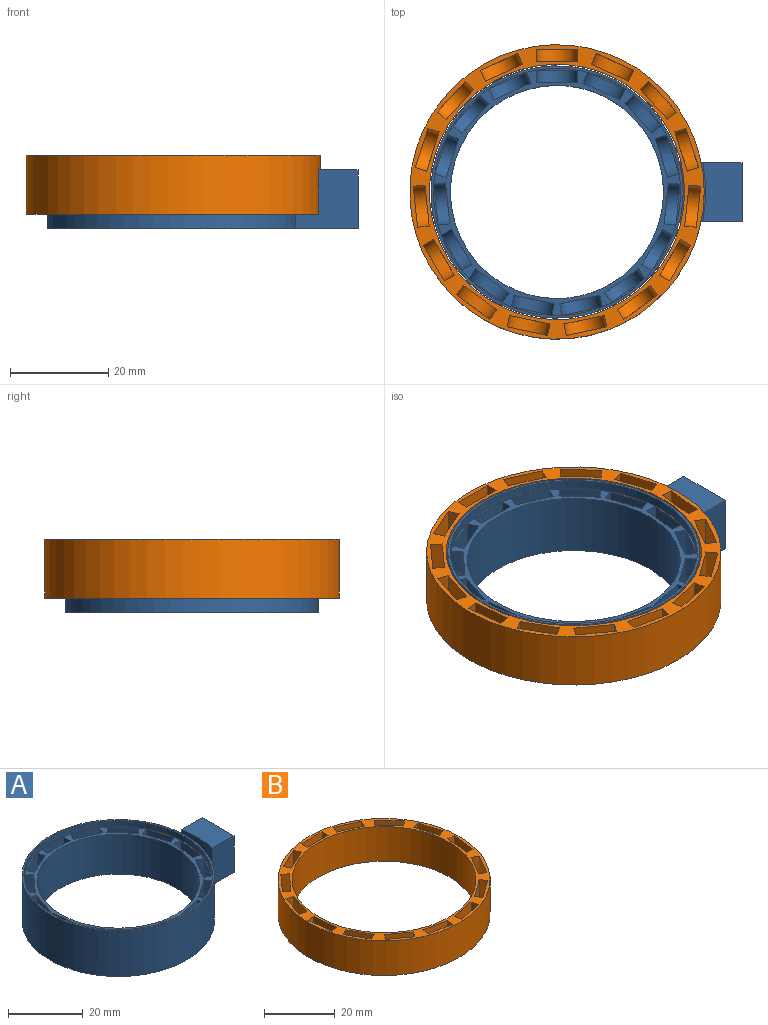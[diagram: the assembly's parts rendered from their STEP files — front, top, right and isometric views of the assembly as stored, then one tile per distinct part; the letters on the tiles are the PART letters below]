
ASSEMBLY  parts=2 mates=1
PART A: 87 faces, bbox 63.4x51.4x15 mm
  f0: cylinder r=21.7mm len=43.4mm, axis (0,0,1), area 1772.5mm2, adj f7,f10
  f1: plane 12x5.31mm, normal (0,0,1), area 55.6mm2, adj f2,f4,f6,f8
  f2: cylinder r=25.7mm len=51.4mm, axis (0,0,-1), area 2385.8mm2, adj f1,f3,f4,f6,f7
  f3: plane 51.4x51.4mm, normal (0,0,1), area 80mm2, adj f2,f11
  f4: plane 12.71x12mm, normal (0,1,0), area 110.1mm2, adj f1,f2,f5,f7,f8,f9
  f5: plane 12x12mm, normal (1,0,0), area 144mm2, adj f4,f6,f7,f9
  f6: plane 12.71x12mm, normal (0,-1,0), area 110.1mm2, adj f1,f2,f5,f7,f8,f9
  f7: plane 63.4x51.4mm, normal (0,0,-1), area 742.5mm2, adj f0,f2,f4,f5,f6
  f8: cylinder r=30.3mm len=12mm, axis (0,0,-1), area 108.7mm2, adj f1,f4,f6,f9
  f9: plane 12x8mm, normal (0,0,1), area 91.2mm2, adj f4,f5,f6,f8
  f10: plane 50.4x50.4mm, normal (0,0,1), area 213.3mm2, adj f0,f11,f13,f14,f15,f16,f18,f19
  f11: cylinder r=25.2mm len=50.4mm, axis (0,0,1), area 316.7mm2, adj f3,f10
  f12: cylinder r=4.2mm len=7.85mm, axis (0.74,0.67,0), area 31.7mm2, adj f13,f14,f15,f16
  f13: plane 9x6.24mm, normal (0.74,0.67,0), area 68mm2, adj f10,f12,f14,f16
  f14: plane 4.8x1.78mm, normal (0.67,-0.74,0), area 11.5mm2, adj f10,f12,f13,f15
  f15: plane 9x6.24mm, normal (-0.74,-0.67,0), area 68mm2, adj f10,f12,f14,f16
  f16: plane 4.8x1.78mm, normal (-0.67,0.74,0), area 11.5mm2, adj f10,f12,f13,f15
  f17: cylinder r=4.2mm len=8.73mm, axis (0.95,0.31,0), area 31.7mm2, adj f18,f19,f20,f21
  f18: plane 9x7.99mm, normal (0.95,0.31,0), area 68mm2, adj f10,f17,f19,f21
  f19: plane 4.8x2.28mm, normal (0.31,-0.95,0), area 11.5mm2, adj f10,f17,f18,f20
  f20: plane 9x7.99mm, normal (-0.95,-0.31,0), area 68mm2, adj f10,f17,f19,f21
  f21: plane 4.8x2.28mm, normal (-0.31,0.95,0), area 11.5mm2, adj f10,f17,f18,f20
  f22: cylinder r=4.2mm len=8.61mm, axis (0.99,-0.1,0), area 31.7mm2, adj f23,f24,f25,f26
  f23: plane 9x8.35mm, normal (0.99,-0.1,0), area 68mm2, adj f10,f22,f24,f26
  f24: plane 4.8x2.39mm, normal (-0.1,-0.99,0), area 11.5mm2, adj f10,f22,f23,f25
  f25: plane 9x8.35mm, normal (-0.99,0.1,0), area 68mm2, adj f10,f22,f24,f26
  f26: plane 4.8x2.39mm, normal (0.1,0.99,0), area 11.5mm2, adj f10,f22,f23,f25
  f27: cylinder r=4.2mm len=8.47mm, axis (0.87,-0.5,0), area 31.7mm2, adj f28,f29,f30,f31
  f28: plane 9x7.27mm, normal (0.87,-0.5,0), area 68mm2, adj f10,f27,f29,f31
  f29: plane 4.8x2.08mm, normal (-0.5,-0.87,0), area 11.5mm2, adj f10,f27,f28,f30
  f30: plane 9x7.27mm, normal (-0.87,0.5,0), area 68mm2, adj f10,f27,f29,f31
  f31: plane 4.8x2.08mm, normal (0.5,0.87,0), area 11.5mm2, adj f10,f27,f28,f30
  f32: cylinder r=4.2mm len=8.21mm, axis (0.59,-0.81,0), area 31.7mm2, adj f33,f34,f35,f36
  f33: plane 9x6.8mm, normal (0.59,-0.81,0), area 68mm2, adj f10,f32,f34,f36
  f34: plane 4.8x1.94mm, normal (-0.81,-0.59,0), area 11.5mm2, adj f10,f32,f33,f35
  f35: plane 9x6.8mm, normal (-0.59,0.81,0), area 68mm2, adj f10,f32,f34,f36
  f36: plane 4.8x1.94mm, normal (0.81,0.59,0), area 11.5mm2, adj f10,f32,f33,f35
  f37: cylinder r=4.2mm len=8.72mm, axis (0.21,-0.98,0), area 31.7mm2, adj f38,f39,f40,f41
  f38: plane 9x8.22mm, normal (0.21,-0.98,0), area 68mm2, adj f10,f37,f39,f41
  f39: plane 4.8x2.35mm, normal (-0.98,-0.21,0), area 11.5mm2, adj f10,f37,f38,f40
  f40: plane 9x8.22mm, normal (-0.21,0.98,0), area 68mm2, adj f10,f37,f39,f41
  f41: plane 4.8x2.35mm, normal (0.98,0.21,0), area 11.5mm2, adj f10,f37,f38,f40
  f42: cylinder r=4.2mm len=8.72mm, axis (-0.21,-0.98,0), area 31.7mm2, adj f43,f44,f45,f46
  f43: plane 9x8.22mm, normal (-0.21,-0.98,0), area 68mm2, adj f10,f42,f44,f46
  f44: plane 4.8x2.35mm, normal (-0.98,0.21,0), area 11.5mm2, adj f10,f42,f43,f45
  f45: plane 9x8.22mm, normal (0.21,0.98,0), area 68mm2, adj f10,f42,f44,f46
  f46: plane 4.8x2.35mm, normal (0.98,-0.21,0), area 11.5mm2, adj f10,f42,f43,f45
  f47: cylinder r=4.2mm len=8.21mm, axis (-0.59,-0.81,0), area 31.7mm2, adj f48,f49,f50,f51
  f48: plane 9x6.8mm, normal (-0.59,-0.81,0), area 68mm2, adj f10,f47,f49,f51
  f49: plane 4.8x1.94mm, normal (-0.81,0.59,0), area 11.5mm2, adj f10,f47,f48,f50
  f50: plane 9x6.8mm, normal (0.59,0.81,0), area 68mm2, adj f10,f47,f49,f51
  f51: plane 4.8x1.94mm, normal (0.81,-0.59,0), area 11.5mm2, adj f10,f47,f48,f50
  f52: cylinder r=4.2mm len=8.47mm, axis (-0.87,-0.5,0), area 31.7mm2, adj f53,f54,f55,f56
  f53: plane 9x7.27mm, normal (-0.87,-0.5,0), area 68mm2, adj f10,f52,f54,f56
  f54: plane 4.8x2.08mm, normal (-0.5,0.87,0), area 11.5mm2, adj f10,f52,f53,f55
  f55: plane 9x7.27mm, normal (0.87,0.5,0), area 68mm2, adj f10,f52,f54,f56
  f56: plane 4.8x2.08mm, normal (0.5,-0.87,0), area 11.5mm2, adj f10,f52,f53,f55
  f57: cylinder r=4.2mm len=8.61mm, axis (-0.99,-0.1,0), area 31.7mm2, adj f58,f59,f60,f61
  f58: plane 9x8.35mm, normal (-0.99,-0.1,0), area 68mm2, adj f10,f57,f59,f61
  f59: plane 4.8x2.39mm, normal (-0.1,0.99,0), area 11.5mm2, adj f10,f57,f58,f60
  f60: plane 9x8.35mm, normal (0.99,0.1,0), area 68mm2, adj f10,f57,f59,f61
  f61: plane 4.8x2.39mm, normal (0.1,-0.99,0), area 11.5mm2, adj f10,f57,f58,f60
  f62: cylinder r=4.2mm len=8.73mm, axis (-0.95,0.31,0), area 31.7mm2, adj f63,f64,f65,f66
  f63: plane 9x7.99mm, normal (-0.95,0.31,0), area 68mm2, adj f10,f62,f64,f66
  f64: plane 4.8x2.28mm, normal (0.31,0.95,0), area 11.5mm2, adj f10,f62,f63,f65
  f65: plane 9x7.99mm, normal (0.95,-0.31,0), area 68mm2, adj f10,f62,f64,f66
  f66: plane 4.8x2.28mm, normal (-0.31,-0.95,0), area 11.5mm2, adj f10,f62,f63,f65
  f67: cylinder r=4.2mm len=7.85mm, axis (-0.74,0.67,0), area 31.7mm2, adj f68,f69,f70,f71
  f68: plane 9x6.24mm, normal (-0.74,0.67,0), area 68mm2, adj f10,f67,f69,f71
  f69: plane 4.8x1.78mm, normal (0.67,0.74,0), area 11.5mm2, adj f10,f67,f68,f70
  f70: plane 9x6.24mm, normal (0.74,-0.67,0), area 68mm2, adj f10,f67,f69,f71
  f71: plane 4.8x1.78mm, normal (-0.67,-0.74,0), area 11.5mm2, adj f10,f67,f68,f70
  f72: cylinder r=4.2mm len=8.65mm, axis (-0.41,0.91,0), area 31.7mm2, adj f73,f74,f75,f76
  f73: plane 9x7.67mm, normal (-0.41,0.91,0), area 68mm2, adj f10,f72,f74,f76
  f74: plane 4.8x2.19mm, normal (0.91,0.41,0), area 11.5mm2, adj f10,f72,f73,f75
  f75: plane 9x7.67mm, normal (0.41,-0.91,0), area 68mm2, adj f10,f72,f74,f76
  f76: plane 4.8x2.19mm, normal (-0.91,-0.41,0), area 11.5mm2, adj f10,f72,f73,f75
  f77: cylinder r=4.2mm len=8.4mm, axis (0,1,0), area 31.7mm2, adj f78,f79,f80,f81
  f78: plane 9x8.4mm, normal (0,1,0), area 68mm2, adj f10,f77,f79,f81
  f79: plane 4.8x2.4mm, normal (1,0,0), area 11.5mm2, adj f10,f77,f78,f80
  f80: plane 9x8.4mm, normal (0,-1,0), area 68mm2, adj f10,f77,f79,f81
  f81: plane 4.8x2.4mm, normal (-1,0,0), area 11.5mm2, adj f10,f77,f78,f80
  f82: cylinder r=4.2mm len=8.65mm, axis (0.41,0.91,0), area 31.7mm2, adj f83,f84,f85,f86
  f83: plane 9x7.67mm, normal (0.41,0.91,0), area 68mm2, adj f10,f82,f84,f86
  f84: plane 4.8x2.19mm, normal (0.91,-0.41,0), area 11.5mm2, adj f10,f82,f83,f85
  f85: plane 9x7.67mm, normal (-0.41,-0.91,0), area 68mm2, adj f10,f82,f84,f86
  f86: plane 4.8x2.19mm, normal (-0.91,0.41,0), area 11.5mm2, adj f10,f82,f83,f85
PART B: 79 faces, bbox 60x60x12 mm
  f0: cylinder r=26mm len=52mm, axis (0,0,-1), area 1960.4mm2, adj f2,f3
  f1: cylinder r=30mm len=60mm, axis (0,0,-1), area 2261.9mm2, adj f2,f3
  f2: plane 60x60mm, normal (0,0,1), area 401.3mm2, adj f0,f1,f4,f5,f6,f7,f9,f10
  f3: plane 60x60mm, normal (0,0,-1), area 703.7mm2, adj f0,f1
  f4: plane 6.8x2.4mm, normal (-1,0,0), area 16.3mm2, adj f2,f5,f7,f8
  f5: plane 11x8.4mm, normal (0,-1,0), area 84.8mm2, adj f2,f4,f6,f8
  f6: plane 6.8x2.4mm, normal (1,0,0), area 16.3mm2, adj f2,f5,f7,f8
  f7: plane 11x8.4mm, normal (0,1,0), area 84.8mm2, adj f2,f4,f6,f8
  f8: cylinder r=4.2mm len=8.4mm, axis (0,1,0), area 31.7mm2, adj f4,f5,f6,f7
  f9: plane 6.8x2.19mm, normal (-0.91,-0.41,0), area 16.3mm2, adj f2,f10,f12,f13
  f10: plane 11x7.67mm, normal (0.41,-0.91,0), area 84.8mm2, adj f2,f9,f11,f13
  f11: plane 6.8x2.19mm, normal (0.91,0.41,0), area 16.3mm2, adj f2,f10,f12,f13
  f12: plane 11x7.67mm, normal (-0.41,0.91,0), area 84.8mm2, adj f2,f9,f11,f13
  f13: cylinder r=4.2mm len=8.65mm, axis (-0.41,0.91,0), area 31.7mm2, adj f9,f10,f11,f12
  f14: plane 6.8x1.78mm, normal (-0.67,-0.74,0), area 16.3mm2, adj f2,f15,f17,f18
  f15: plane 11x6.24mm, normal (0.74,-0.67,0), area 84.8mm2, adj f2,f14,f16,f18
  f16: plane 6.8x1.78mm, normal (0.67,0.74,0), area 16.3mm2, adj f2,f15,f17,f18
  f17: plane 11x6.24mm, normal (-0.74,0.67,0), area 84.8mm2, adj f2,f14,f16,f18
  f18: cylinder r=4.2mm len=7.85mm, axis (-0.74,0.67,0), area 31.7mm2, adj f14,f15,f16,f17
  f19: plane 6.8x2.28mm, normal (-0.31,-0.95,0), area 16.3mm2, adj f2,f20,f22,f23
  f20: plane 11x7.99mm, normal (0.95,-0.31,0), area 84.8mm2, adj f2,f19,f21,f23
  f21: plane 6.8x2.28mm, normal (0.31,0.95,0), area 16.3mm2, adj f2,f20,f22,f23
  f22: plane 11x7.99mm, normal (-0.95,0.31,0), area 84.8mm2, adj f2,f19,f21,f23
  f23: cylinder r=4.2mm len=8.73mm, axis (-0.95,0.31,0), area 31.7mm2, adj f19,f20,f21,f22
  f24: plane 6.8x2.39mm, normal (0.1,-0.99,0), area 16.3mm2, adj f2,f25,f27,f28
  f25: plane 11x8.35mm, normal (0.99,0.1,0), area 84.8mm2, adj f2,f24,f26,f28
  f26: plane 6.8x2.39mm, normal (-0.1,0.99,0), area 16.3mm2, adj f2,f25,f27,f28
  f27: plane 11x8.35mm, normal (-0.99,-0.1,0), area 84.8mm2, adj f2,f24,f26,f28
  f28: cylinder r=4.2mm len=8.61mm, axis (-0.99,-0.1,0), area 31.7mm2, adj f24,f25,f26,f27
  f29: plane 6.8x2.08mm, normal (0.5,-0.87,0), area 16.3mm2, adj f2,f30,f32,f33
  f30: plane 11x7.27mm, normal (0.87,0.5,0), area 84.8mm2, adj f2,f29,f31,f33
  f31: plane 6.8x2.08mm, normal (-0.5,0.87,0), area 16.3mm2, adj f2,f30,f32,f33
  f32: plane 11x7.27mm, normal (-0.87,-0.5,0), area 84.8mm2, adj f2,f29,f31,f33
  f33: cylinder r=4.2mm len=8.47mm, axis (-0.87,-0.5,0), area 31.7mm2, adj f29,f30,f31,f32
  f34: plane 6.8x1.94mm, normal (0.81,-0.59,0), area 16.3mm2, adj f2,f35,f37,f38
  f35: plane 11x6.8mm, normal (0.59,0.81,0), area 84.8mm2, adj f2,f34,f36,f38
  f36: plane 6.8x1.94mm, normal (-0.81,0.59,0), area 16.3mm2, adj f2,f35,f37,f38
  f37: plane 11x6.8mm, normal (-0.59,-0.81,0), area 84.8mm2, adj f2,f34,f36,f38
  f38: cylinder r=4.2mm len=8.21mm, axis (-0.59,-0.81,0), area 31.7mm2, adj f34,f35,f36,f37
  f39: plane 6.8x2.35mm, normal (0.98,-0.21,0), area 16.3mm2, adj f2,f40,f42,f43
  f40: plane 11x8.22mm, normal (0.21,0.98,0), area 84.8mm2, adj f2,f39,f41,f43
  f41: plane 6.8x2.35mm, normal (-0.98,0.21,0), area 16.3mm2, adj f2,f40,f42,f43
  f42: plane 11x8.22mm, normal (-0.21,-0.98,0), area 84.8mm2, adj f2,f39,f41,f43
  f43: cylinder r=4.2mm len=8.72mm, axis (-0.21,-0.98,0), area 31.7mm2, adj f39,f40,f41,f42
  f44: plane 6.8x2.35mm, normal (0.98,0.21,0), area 16.3mm2, adj f2,f45,f47,f48
  f45: plane 11x8.22mm, normal (-0.21,0.98,0), area 84.8mm2, adj f2,f44,f46,f48
  f46: plane 6.8x2.35mm, normal (-0.98,-0.21,0), area 16.3mm2, adj f2,f45,f47,f48
  f47: plane 11x8.22mm, normal (0.21,-0.98,0), area 84.8mm2, adj f2,f44,f46,f48
  f48: cylinder r=4.2mm len=8.72mm, axis (0.21,-0.98,0), area 31.7mm2, adj f44,f45,f46,f47
  f49: plane 6.8x1.94mm, normal (0.81,0.59,0), area 16.3mm2, adj f2,f50,f52,f53
  f50: plane 11x6.8mm, normal (-0.59,0.81,0), area 84.8mm2, adj f2,f49,f51,f53
  f51: plane 6.8x1.94mm, normal (-0.81,-0.59,0), area 16.3mm2, adj f2,f50,f52,f53
  f52: plane 11x6.8mm, normal (0.59,-0.81,0), area 84.8mm2, adj f2,f49,f51,f53
  f53: cylinder r=4.2mm len=8.21mm, axis (0.59,-0.81,0), area 31.7mm2, adj f49,f50,f51,f52
  f54: plane 6.8x2.08mm, normal (0.5,0.87,0), area 16.3mm2, adj f2,f55,f57,f58
  f55: plane 11x7.27mm, normal (-0.87,0.5,0), area 84.8mm2, adj f2,f54,f56,f58
  f56: plane 6.8x2.08mm, normal (-0.5,-0.87,0), area 16.3mm2, adj f2,f55,f57,f58
  f57: plane 11x7.27mm, normal (0.87,-0.5,0), area 84.8mm2, adj f2,f54,f56,f58
  f58: cylinder r=4.2mm len=8.47mm, axis (0.87,-0.5,0), area 31.7mm2, adj f54,f55,f56,f57
  f59: plane 6.8x2.39mm, normal (0.1,0.99,0), area 16.3mm2, adj f2,f60,f62,f63
  f60: plane 11x8.35mm, normal (-0.99,0.1,0), area 84.8mm2, adj f2,f59,f61,f63
  f61: plane 6.8x2.39mm, normal (-0.1,-0.99,0), area 16.3mm2, adj f2,f60,f62,f63
  f62: plane 11x8.35mm, normal (0.99,-0.1,0), area 84.8mm2, adj f2,f59,f61,f63
  f63: cylinder r=4.2mm len=8.61mm, axis (0.99,-0.1,0), area 31.7mm2, adj f59,f60,f61,f62
  f64: plane 6.8x2.28mm, normal (-0.31,0.95,0), area 16.3mm2, adj f2,f65,f67,f68
  f65: plane 11x7.99mm, normal (-0.95,-0.31,0), area 84.8mm2, adj f2,f64,f66,f68
  f66: plane 6.8x2.28mm, normal (0.31,-0.95,0), area 16.3mm2, adj f2,f65,f67,f68
  f67: plane 11x7.99mm, normal (0.95,0.31,0), area 84.8mm2, adj f2,f64,f66,f68
  f68: cylinder r=4.2mm len=8.73mm, axis (0.95,0.31,0), area 31.7mm2, adj f64,f65,f66,f67
  f69: plane 6.8x1.78mm, normal (-0.67,0.74,0), area 16.3mm2, adj f2,f70,f72,f73
  f70: plane 11x6.24mm, normal (-0.74,-0.67,0), area 84.8mm2, adj f2,f69,f71,f73
  f71: plane 6.8x1.78mm, normal (0.67,-0.74,0), area 16.3mm2, adj f2,f70,f72,f73
  f72: plane 11x6.24mm, normal (0.74,0.67,0), area 84.8mm2, adj f2,f69,f71,f73
  f73: cylinder r=4.2mm len=7.85mm, axis (0.74,0.67,0), area 31.7mm2, adj f69,f70,f71,f72
  f74: plane 6.8x2.19mm, normal (-0.91,0.41,0), area 16.3mm2, adj f2,f75,f77,f78
  f75: plane 11x7.67mm, normal (-0.41,-0.91,0), area 84.8mm2, adj f2,f74,f76,f78
  f76: plane 6.8x2.19mm, normal (0.91,-0.41,0), area 16.3mm2, adj f2,f75,f77,f78
  f77: plane 11x7.67mm, normal (0.41,0.91,0), area 84.8mm2, adj f2,f74,f76,f78
  f78: cylinder r=4.2mm len=8.65mm, axis (0.41,0.91,0), area 31.7mm2, adj f74,f75,f76,f77
PLACE A t=(-14.54,-1.76,3.95)mm
PLACE B t=(-14.54,-1.76,3.95)mm fixed
MATE slider A.f0 <-> B.f0  axis (0,0,-1) through (-14.54,-1.76,8.45)mm
